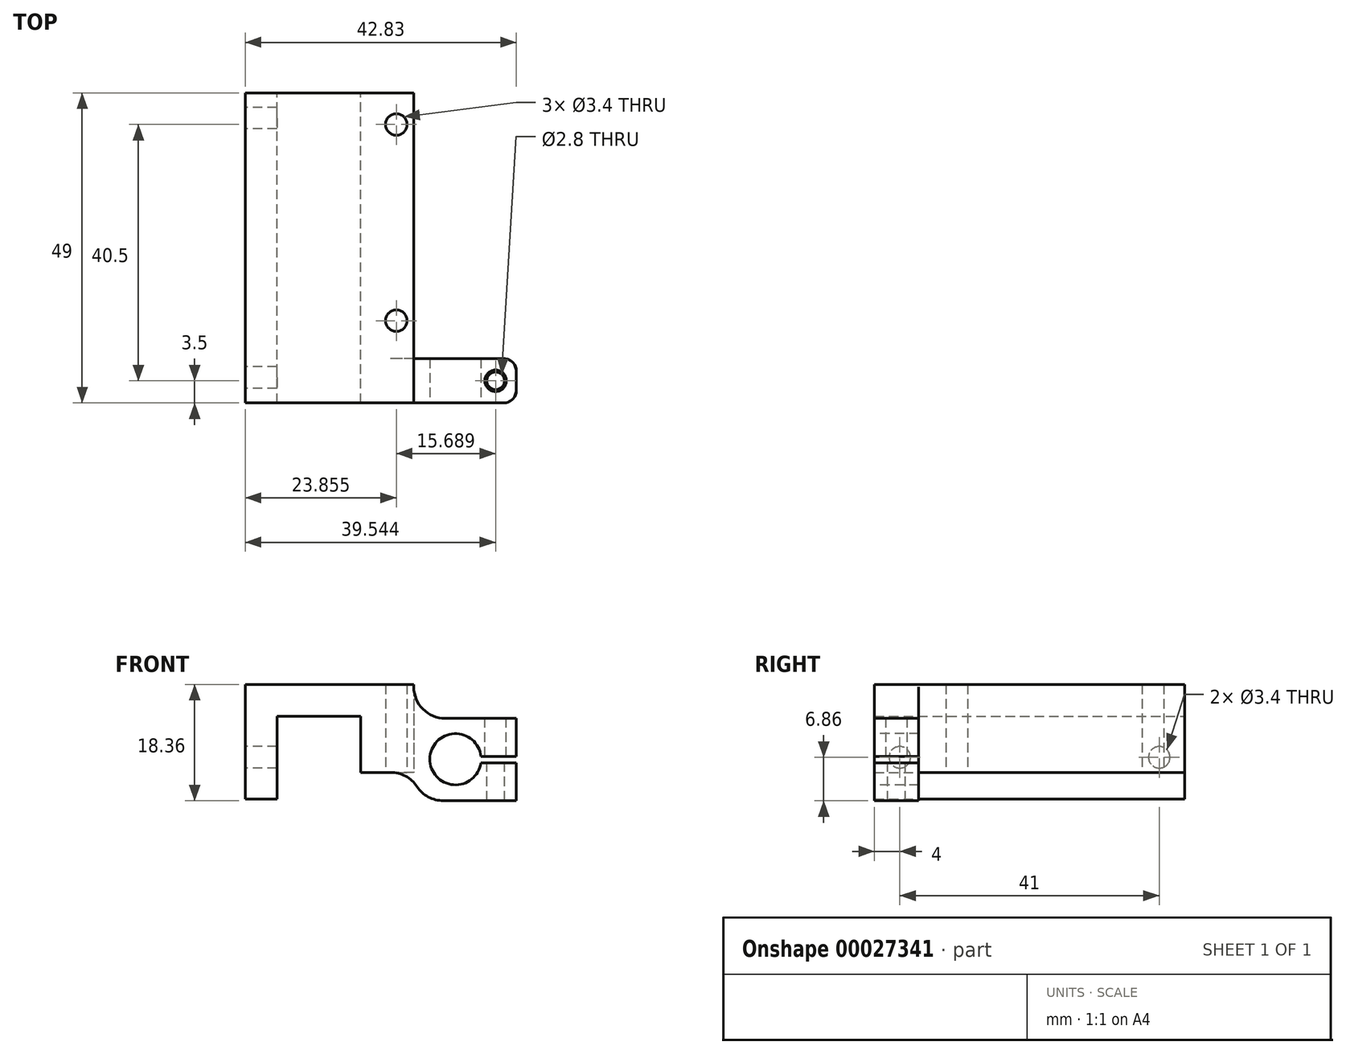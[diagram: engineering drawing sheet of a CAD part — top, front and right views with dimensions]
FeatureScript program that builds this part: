
annotation { "Feature Type Name" : "Feature", "Feature Type Description" : "" }
export const myFeature = defineFeature(function(context is Context, id is Id, definition is map)
    precondition{}
    {
        {
            var Q0;
            Q0=qCreatedBy(makeId("Front.planeOp"),FACE);
            var sketch = newSketch(context, id + "F0", { "sketchPlane" : qUnion([Q0])});
            skLineSegment(sketch, "E0", {"start": v(-21.67, 4.6) * mm, "end": v(-21.67, 22.7) * mm});
            skLineSegment(sketch, "E1", {"start": v(-21.67, 22.7) * mm, "end": v(4.94, 22.7) * mm});
            skLineSegment(sketch, "E2", {"start": v(4.94, 22.7) * mm, "end": v(4.94, 17.34) * mm});
            skLineSegment(sketch, "E3", {"start": v(-3.47, 8.8) * mm, "end": v(-3.47, 17.7) * mm});
            skLineSegment(sketch, "E4", {"start": v(-3.47, 17.7) * mm, "end": v(-16.67, 17.7) * mm});
            skLineSegment(sketch, "E5", {"start": v(-16.67, 17.7) * mm, "end": v(-16.67, 4.6) * mm});
            skLineSegment(sketch, "E6", {"start": v(-16.67, 4.6) * mm, "end": v(-21.67, 4.6) * mm});
            skLineSegment(sketch, "E7", {"start": v(4.94, 17.34) * mm, "end": v(4.94, 8.8) * mm});
            skLineSegment(sketch, "E8", {"start": v(4.94, 8.8) * mm, "end": v(-3.47, 8.8) * mm});
            skLineSegment(sketch, "E9", {"start": v(4.94, 17.34) * mm, "end": v(4.94, 17.34) * mm});
            skLineSegment(sketch, "E10", {"start": v(21.13, 11.34) * mm, "end": v(13.49, 11.34) * mm});
            skLineSegment(sketch, "E11", {"start": v(13.49, 11.34) * mm, "end": v(13.49, 10.34) * mm});
            skLineSegment(sketch, "E12", {"start": v(13.49, 10.34) * mm, "end": v(21.16, 10.34) * mm});
            skLineSegment(sketch, "E13", {"start": v(21.16, 10.34) * mm, "end": v(21.16, 4.34) * mm});
            skLineSegment(sketch, "E14", {"start": v(21.16, 4.34) * mm, "end": v(6.35, 4.34) * mm});
            skLineSegment(sketch, "E15", {"start": v(6.35, 4.34) * mm, "end": v(4.94, 8.8) * mm});
            skLineSegment(sketch, "E16", {"start": v(21.13, 17.34) * mm, "end": v(4.94, 17.34) * mm});
            skLineSegment(sketch, "E17", {"start": v(21.13, 17.34) * mm, "end": v(21.13, 11.34) * mm});
            skSolve(sketch);
        }
        {
            var Q0;
            Q0=makeQuery(id+"F0.imprint","IMPRINT",FACE,{"disambiguationData":[TD([[makeQuery(id+"F0.imprint","IMPRINT",EDGE,{"derivedFrom":sQuery(id+"F0.wireOp",EDGE,"E0")}),-1.0]])]});
            var Q1;
            {var subQ2=sQuery(id+"F0.wireOp",EDGE,"69cbcc5d-e0c3-48db-8baf-3487a8abab7d");Q1=makeQuery(id+"F0.imprint","IMPRINT",FACE,{"disambiguationData":[TD([[makeQuery(id+"F0.imprint","IMPRINT",EDGE,{"derivedFrom":subQ2}),-1.0]])]});}
            var Q2;
            Q2=makeQuery(id+"F0.imprint","IMPRINT",FACE,{"disambiguationData":[TD([[makeQuery(id+"F0.imprint","IMPRINT",EDGE,{"derivedFrom":sQuery(id+"F0.wireOp",EDGE,"E7")}),1.0]])]});
            extrude(context, id + "F1", {"entities" : qUnion([Q0, Q1, Q2]), "depth" : 7 * mm});
        }
        {
            var Q0;
            Q0=makeQuery(id+"F0.imprint","IMPRINT",FACE,{"disambiguationData":[TD([[makeQuery(id+"F0.imprint","IMPRINT",EDGE,{"derivedFrom":sQuery(id+"F0.wireOp",EDGE,"E0")}),-1.0]])]});
            extrude(context, id + "F2", {"entities" : qUnion([Q0]), "operationType" : NewBodyOperationType.ADD, "oppositeDirection" : true, "depth" : 42 * mm});
        }
        {
            var Q0;
            {var subQ0=sQuery(id+"F0.wireOp",EDGE,"E8");Q0=makeQuery(id+"F2.boolean.opBoolean","MERGE",FACE,{"derivedFrom":[makeQuery(id+"F1.opExtrude","SWEPT_FACE",FACE,{"disambiguationData":[OSD([subQ0])]}),makeQuery(id+"F2.opExtrude","SWEPT_FACE",FACE,{"disambiguationData":[OSD([subQ0])]})]});}
            var sketch = newSketch(context, id + "F3", { "sketchPlane" : qUnion([Q0])});
            skCircle(sketch, "E18", {"center": v(2.19, -6) * mm, "radius": 1.7 * mm});
            skCircle(sketch, "E19", {"center": v(2.19, -37) * mm, "radius": 1.7 * mm});
            skCircle(sketch, "E20", {"center": v(17.69, -21.5) * mm, "radius": 11 * mm});
            skSolve(sketch);
        }
        {
            var Q0;
            Q0=qSketchRegion(id+"F3",true);
            extrude(context, id + "F4", {"entities" : qUnion([Q0]), "operationType" : NewBodyOperationType.REMOVE, "endBound" : BoundingType.THROUGH_ALL, "oppositeDirection" : true, "depth" : 25 * mm});
        }
        {
            var Q0;
            Q0=makeQuery(id+"F1.opExtrude","CAP_FACE",FACE,{"disambiguationData":[OSD([sQuery(id+"F0.wireOp",EDGE,"E0"),sQuery(id+"F0.wireOp",EDGE,"E1"),sQuery(id+"F0.wireOp",EDGE,"E2"),sQuery(id+"F0.wireOp",EDGE,"E3"),sQuery(id+"F0.wireOp",EDGE,"E4"),sQuery(id+"F0.wireOp",EDGE,"E5"),sQuery(id+"F0.wireOp",EDGE,"E6"),sQuery(id+"F0.wireOp",EDGE,"E8"),sQuery(id+"F0.wireOp",EDGE,"E9"),sQuery(id+"F0.wireOp",EDGE,"58f11638-63e7-4b32-8aff-a1ba3c53649b"),sQuery(id+"F0.wireOp",EDGE,"26189fee-d4a5-4195-b7cd-97af38bcc1d7"),sQuery(id+"F0.wireOp",EDGE,"E10"),sQuery(id+"F0.wireOp",EDGE,"E11"),sQuery(id+"F0.wireOp",EDGE,"E12"),sQuery(id+"F0.wireOp",EDGE,"E13"),sQuery(id+"F0.wireOp",EDGE,"E14"),sQuery(id+"F0.wireOp",EDGE,"E15")])],"isStart":false});
            var sketch = newSketch(context, id + "F5", { "sketchPlane" : qUnion([Q0])});
            skCircle(sketch, "E21", {"center": v(11.53, 10.9) * mm, "radius": 4.05 * mm});
            skSolve(sketch);
        }
        {
            var Q0;
            Q0=qSketchRegion(id+"F5",true);
            extrude(context, id + "F6", {"entities" : qUnion([Q0]), "operationType" : NewBodyOperationType.REMOVE, "oppositeDirection" : true, "depth" : 10 * mm});
        }
        {
            var Q0;
            Q0=qSketchRegion(id+"F3",true);
            extrude(context, id + "F7", {"entities" : qUnion([Q0]), "operationType" : NewBodyOperationType.REMOVE, "endBound" : BoundingType.THROUGH_ALL, "oppositeDirection" : true, "depth" : 25 * mm});
        }
        {
            var Q0;
            Q0=makeQuery(id+"F1.opExtrude","SWEPT_FACE",FACE,{"disambiguationData":[OSD([sQuery(id+"F0.wireOp",EDGE,"E16")])]});
            var sketch = newSketch(context, id + "F8", { "sketchPlane" : qUnion([Q0])});
            skCircle(sketch, "E22", {"center": v(17.87, -3.5) * mm, "radius": 1.7 * mm});
            skCircle(sketch, "E23", {"center": v(17.87, -3.5) * mm, "radius": 1.4 * mm});
            skSolve(sketch);
        }
        {
            var Q0;
            Q0=makeQuery(id+"F8.imprint","IMPRINT",FACE,{"disambiguationData":[TD([[makeQuery(id+"F8.imprint","IMPRINT",EDGE,{"derivedFrom":sQuery(id+"F8.wireOp",EDGE,"E23")}),1.0]])]});
            extrude(context, id + "F9", {"entities" : qUnion([Q0]), "operationType" : NewBodyOperationType.REMOVE, "endBound" : BoundingType.THROUGH_ALL, "oppositeDirection" : true, "depth" : 25 * mm});
        }
        {
            var Q0;
            Q0=makeQuery(id+"F8.imprint","IMPRINT",FACE,{"disambiguationData":[TD([[makeQuery(id+"F8.imprint","IMPRINT",EDGE,{"derivedFrom":sQuery(id+"F8.wireOp",EDGE,"E22")}),1.0]])]});
            extrude(context, id + "F10", {"entities" : qUnion([Q0]), "operationType" : NewBodyOperationType.REMOVE, "endBound" : BoundingType.UP_TO_NEXT, "oppositeDirection" : true, "depth" : 25 * mm});
        }
        {
            var Q0;
            Q0=makeQuery(id+"F1.opExtrude","SWEPT_EDGE",EDGE,{"disambiguationData":[OSD([sQuery(id+"F0.wireOp",EDGE,"E2"),sQuery(id+"F0.wireOp",EDGE,"E7"),sQuery(id+"F0.wireOp",EDGE,"E16")])]});
            fillet(context, id + "F11", {"entities" : qUnion([Q0]), "radius" : 5 * mm, "tangentPropagation" : true, "allowEdgeOverflow" : false});
        }
        {
            var Q0;
            Q0=makeQuery(id+"F1.opExtrude","SWEPT_EDGE",EDGE,{"disambiguationData":[OSD([sQuery(id+"F0.wireOp",EDGE,"E7"),sQuery(id+"F0.wireOp",EDGE,"E8"),sQuery(id+"F0.wireOp",EDGE,"E15")])]});
            fillet(context, id + "F12", {"entities" : qUnion([Q0]), "radius" : 5 * mm, "tangentPropagation" : true, "allowEdgeOverflow" : false});
        }
        {
            var Q0;
            Q0=makeQuery(id+"F1.opExtrude","SWEPT_EDGE",EDGE,{"disambiguationData":[OSD([sQuery(id+"F0.wireOp",EDGE,"E14"),sQuery(id+"F0.wireOp",EDGE,"E15")])]});
            fillet(context, id + "F13", {"entities" : qUnion([Q0]), "radius" : 5 * mm, "tangentPropagation" : true, "allowEdgeOverflow" : false});
        }
        {
            var Q0;
            Q0=makeQuery(id+"F1.opExtrude","CAP_EDGE",EDGE,{"disambiguationData":[OSD([sQuery(id+"F0.wireOp",EDGE,"26189fee-d4a5-4195-b7cd-97af38bcc1d7")])],"isStart":false});
            var Q1;
            Q1=makeQuery(id+"F1.opExtrude","CAP_EDGE",EDGE,{"disambiguationData":[OSD([sQuery(id+"F0.wireOp",EDGE,"E13")])],"isStart":false});
            var Q2;
            Q2=makeQuery(id+"F1.opExtrude","CAP_EDGE",EDGE,{"disambiguationData":[OSD([sQuery(id+"F0.wireOp",EDGE,"26189fee-d4a5-4195-b7cd-97af38bcc1d7")])],"isStart":true});
            var Q3;
            Q3=makeQuery(id+"F1.opExtrude","CAP_EDGE",EDGE,{"disambiguationData":[OSD([sQuery(id+"F0.wireOp",EDGE,"E13")])],"isStart":true});
            fillet(context, id + "F14", {"entities" : qUnion([Q0, Q1, Q2, Q3]), "radius" : 2 * mm, "tangentPropagation" : true, "allowEdgeOverflow" : false});
        }
        {
            var Q0;
            {var subQ0=sQuery(id+"F0.wireOp",EDGE,"E0");Q0=makeQuery(id+"F2.boolean.opBoolean","MERGE",FACE,{"derivedFrom":[makeQuery(id+"F1.opExtrude","SWEPT_FACE",FACE,{"disambiguationData":[OSD([subQ0])]}),makeQuery(id+"F2.opExtrude","SWEPT_FACE",FACE,{"disambiguationData":[OSD([subQ0])]})]});}
            var sketch = newSketch(context, id + "F15", { "sketchPlane" : qUnion([Q0])});
            skCircle(sketch, "E24", {"center": v(-38, 11.2) * mm, "radius": 1.7 * mm});
            skCircle(sketch, "E25", {"center": v(3, 11.2) * mm, "radius": 1.7 * mm});
            skSolve(sketch);
        }
        {
            var Q0;
            Q0=qSketchRegion(id+"F15",true);
            extrude(context, id + "F16", {"entities" : qUnion([Q0]), "operationType" : NewBodyOperationType.REMOVE, "oppositeDirection" : true, "depth" : 6 * mm});
        }
        {
            var Q0;
            Q0=makeQuery(id+"F1.opExtrude","CAP_EDGE",EDGE,{"disambiguationData":[OSD([sQuery(id+"F0.wireOp",EDGE,"E17")])],"isStart":false});
            var Q1;
            Q1=makeQuery(id+"F1.opExtrude","CAP_EDGE",EDGE,{"disambiguationData":[OSD([sQuery(id+"F0.wireOp",EDGE,"E17")])],"isStart":true});
            fillet(context, id + "F17", {"entities" : qUnion([Q0, Q1]), "radius" : 2 * mm, "tangentPropagation" : true, "allowEdgeOverflow" : false});
        }
    });
